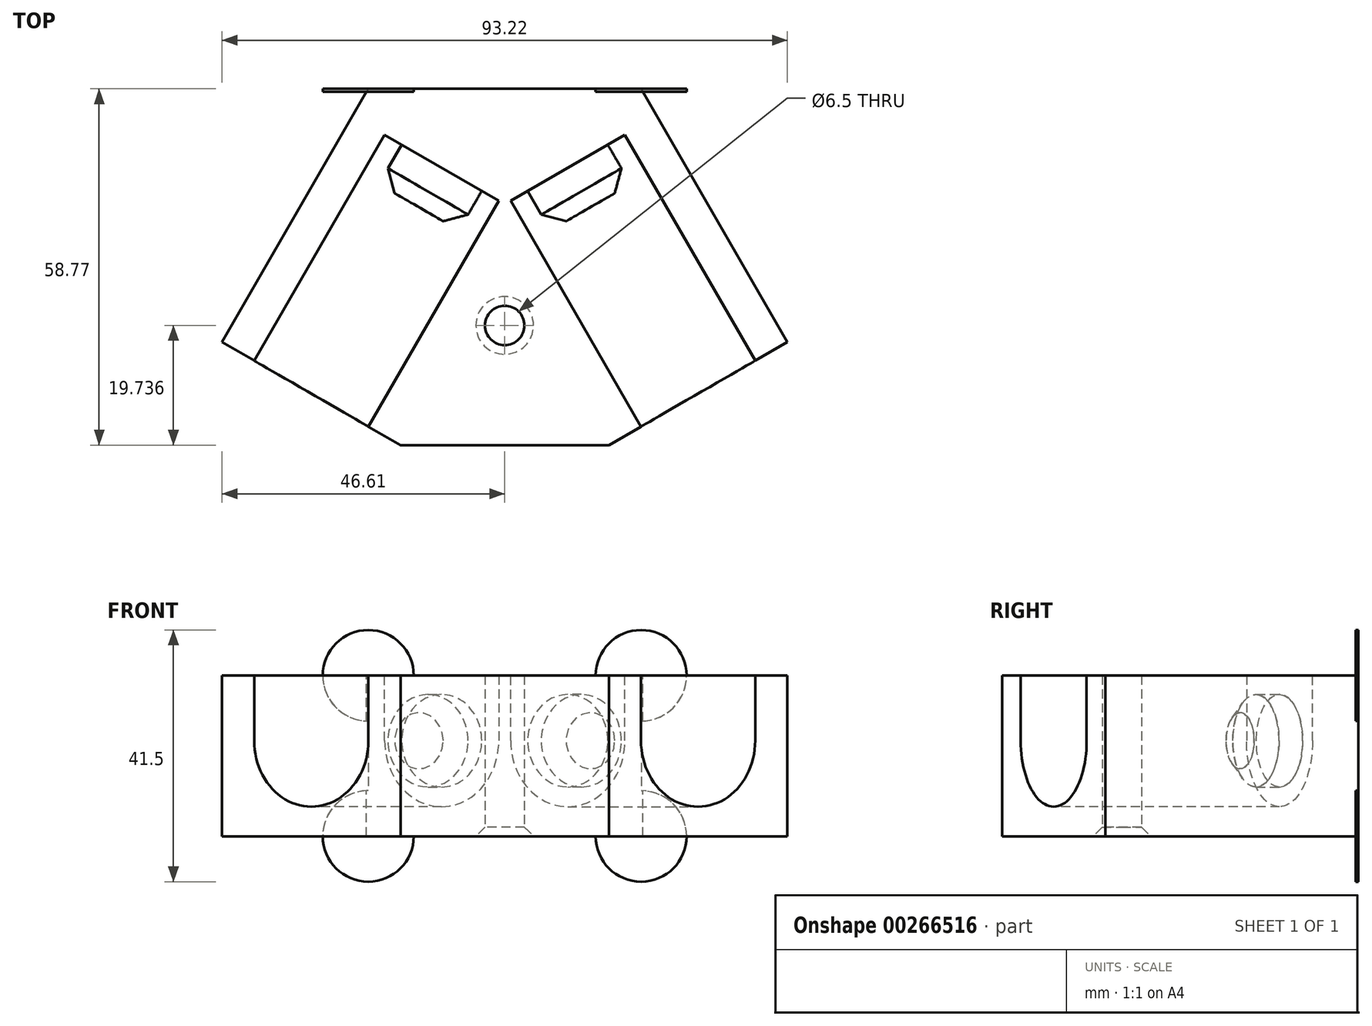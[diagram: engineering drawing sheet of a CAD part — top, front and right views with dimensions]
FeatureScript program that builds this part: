
annotation { "Feature Type Name" : "Feature", "Feature Type Description" : "" }
export const myFeature = defineFeature(function(context is Context, id is Id, definition is map)
    precondition{}
    {
        {
            var Q0;
            Q0=qCreatedBy(makeId("Top.planeOp"),FACE);
            var sketch = newSketch(context, id + "F0", { "sketchPlane" : qUnion([Q0])});
            skCircle(sketch, "E0", {"center": v(0, 0) * mm, "radius": 199.98 * mm, "construction": true});
            skLineSegment(sketch, "E1", {"start": v(0, 199.98) * mm, "end": v(-173.18, -99.99) * mm, "construction": true});
            skLineSegment(sketch, "E2", {"start": v(-173.18, -99.99) * mm, "end": v(173.18, -99.99) * mm, "construction": true});
            skLineSegment(sketch, "E3", {"start": v(173.18, -99.99) * mm, "end": v(0, 199.98) * mm, "construction": true});
            skLineSegment(sketch, "E4", {"start": v(0, 0) * mm, "end": v(-173.18, -99.99) * mm, "construction": true});
            skLineSegment(sketch, "E5", {"start": v(-152.4, -87.99) * mm, "end": v(-152.4, -99.99) * mm, "construction": true});
            skLineSegment(sketch, "E6", {"start": v(-152.4, -87.99) * mm, "end": v(0, -87.99) * mm, "construction": true});
            skLineSegment(sketch, "E7", {"start": v(0, -87.99) * mm, "end": v(0, 0) * mm, "construction": true});
            skLineSegment(sketch, "E8", {"start": v(0, 199.98) * mm, "end": v(0, 0) * mm, "construction": true});
            skLineSegment(sketch, "E9", {"start": v(-20.78, 187.98) * mm, "end": v(0, 175.98) * mm, "construction": true});
            skLineSegment(sketch, "E10", {"start": v(-20.78, 187.98) * mm, "end": v(-42.28, 150.74) * mm, "construction": true});
            skCircle(sketch, "E11", {"center": v(0, 155.98) * mm, "radius": 3.25 * mm});
            skLineSegment(sketch, "E12", {"start": v(0, 175.98) * mm, "end": v(-28.23, 127.08) * mm, "construction": true});
            skLineSegment(sketch, "E13", {"start": v(-22.5, 195) * mm, "end": v(-46.61, 153.24) * mm});
            skLineSegment(sketch, "E14", {"start": v(-46.61, 153.24) * mm, "end": v(-17.17, 136.24) * mm});
            skLineSegment(sketch, "E15.MirrorCS", {"start": v(46.61, 153.24) * mm, "end": v(17.17, 136.24) * mm});
            skLineSegment(sketch, "E16.MirrorCS", {"start": v(22.5, 195) * mm, "end": v(46.61, 153.24) * mm});
            skLineSegment(sketch, "E17", {"start": v(-22.5, 195) * mm, "end": v(22.5, 195) * mm});
            skLineSegment(sketch, "E18", {"start": v(-17.17, 136.24) * mm, "end": v(17.17, 136.24) * mm});
            skSolve(sketch);
        }
        {
            var Q0;
            Q0 = qSketchRegion(id + "F0", true);
            extrude(context, id + "F1", {"entities" : qUnion([Q0]), "depth" : 31.5 * mm});
        }
        {
            var Q0;
            Q0=makeQuery(id+"F1.opExtrude","SWEPT_FACE",FACE,{"disambiguationData":[OSD([sQuery(id+"F0.wireOp",EDGE,"E14")])]});
            var sketch = newSketch(context, id + "F2", { "sketchPlane" : qUnion([Q0])});
            skLineSegment(sketch, "E19", {"start": v(-99.99, 31.5) * mm, "end": v(-99.99, 0) * mm, "construction": true});
            skArc(sketch, "E20", {"start": v(-110.86, 15.75) * mm, "mid": v(-99.99, 4.87) * mm, "end": v(-89.11, 15.75) * mm});
            skPoint(sketch, "E20.startSnap0", {"position": v(-99.99, 15.75) * mm});
            skLineSegment(sketch, "E21", {"start": v(-110.86, 15.75) * mm, "end": v(-110.86, 31.5) * mm});
            skLineSegment(sketch, "E22", {"start": v(-110.86, 31.5) * mm, "end": v(-89.11, 31.5) * mm});
            skLineSegment(sketch, "E23", {"start": v(-89.11, 31.5) * mm, "end": v(-89.11, 15.75) * mm});
            skSolve(sketch);
        }
        {
            var Q0;
            Q0 = qSketchRegion(id + "F2", true);
            extrude(context, id + "F3", {"entities" : qUnion([Q0]), "operationType" : NewBodyOperationType.REMOVE, "oppositeDirection" : true, "depth" : 43 * mm});
        }
        {
            var Q0;
            Q0=makeQuery(id+"F1.opExtrude","SWEPT_FACE",FACE,{"disambiguationData":[OSD([sQuery(id+"F0.wireOp",EDGE,"E15.MirrorCS")])]});
            var sketch = newSketch(context, id + "F4", { "sketchPlane" : qUnion([Q0])});
            skLineSegment(sketch, "E24", {"start": v(99.99, 31.5) * mm, "end": v(99.99, 0) * mm, "construction": true});
            skArc(sketch, "E25", {"start": v(89.11, 15.75) * mm, "mid": v(99.99, 4.87) * mm, "end": v(110.86, 15.75) * mm});
            skPoint(sketch, "E25.startSnap0", {"position": v(99.99, 15.75) * mm});
            skLineSegment(sketch, "E26", {"start": v(89.11, 15.75) * mm, "end": v(89.11, 31.5) * mm});
            skLineSegment(sketch, "E27.MirrorCS", {"start": v(110.86, 15.75) * mm, "end": v(110.86, 31.5) * mm});
            skLineSegment(sketch, "E28", {"start": v(89.11, 31.5) * mm, "end": v(110.86, 31.5) * mm});
            skSolve(sketch);
        }
        {
            var Q0;
            Q0 = qSketchRegion(id + "F4", true);
            extrude(context, id + "F5", {"entities" : qUnion([Q0]), "operationType" : NewBodyOperationType.REMOVE, "oppositeDirection" : true, "depth" : 43 * mm});
        }
        {
            var Q0;
            Q0=makeQuery(id+"F3.boolean.opBoolean","COPY",FACE,{"derivedFrom":makeQuery(id+"F3.opExtrude","CAP_FACE",FACE,{"disambiguationData":[OSD([sQuery(id+"F2.wireOp",EDGE,"E20"),sQuery(id+"F2.wireOp",EDGE,"E21"),sQuery(id+"F2.wireOp",EDGE,"E22"),sQuery(id+"F2.wireOp",EDGE,"E23")])],"isStart":false})});
            var sketch = newSketch(context, id + "F6", { "sketchPlane" : qUnion([Q0])});
            skCircle(sketch, "E29", {"center": v(-99.99, 15.75) * mm, "radius": 7.62 * mm});
            skSolve(sketch);
        }
        {
            var Q0;
            Q0 = qSketchRegion(id + "F6", true);
            extrude(context, id + "F7", {"entities" : qUnion([Q0]), "operationType" : NewBodyOperationType.ADD, "depth" : 7.5 * mm});
        }
        {
            var Q0;
            Q0=makeQuery(id+"F5.boolean.opBoolean","COPY",FACE,{"derivedFrom":makeQuery(id+"F5.opExtrude","CAP_FACE",FACE,{"disambiguationData":[OSD([sQuery(id+"F4.wireOp",EDGE,"E25"),sQuery(id+"F4.wireOp",EDGE,"E26"),sQuery(id+"F4.wireOp",EDGE,"E27.MirrorCS"),sQuery(id+"F4.wireOp",EDGE,"E28")])],"isStart":false})});
            var sketch = newSketch(context, id + "F8", { "sketchPlane" : qUnion([Q0])});
            skCircle(sketch, "E30", {"center": v(99.99, 15.75) * mm, "radius": 7.62 * mm});
            skSolve(sketch);
        }
        {
            var Q0;
            Q0 = qSketchRegion(id + "F8", true);
            extrude(context, id + "F9", {"entities" : qUnion([Q0]), "operationType" : NewBodyOperationType.ADD, "depth" : 7.5 * mm});
        }
        {
            var Q0;
            Q0=makeQuery(id+"F7.opExtrude","CAP_EDGE",EDGE,{"disambiguationData":[OSD([sQuery(id+"F6.wireOp",EDGE,"E29")])],"isStart":false});
            var Q1;
            Q1=makeQuery(id+"F9.opExtrude","CAP_EDGE",EDGE,{"disambiguationData":[OSD([sQuery(id+"F8.wireOp",EDGE,"E30")])],"isStart":false});
            chamfer(context, id + "F10", {"entities" : qUnion([Q0, Q1]), "width" : 3 * mm, "tangentPropagation" : true});
        }
        {
            var Q0;
            Q0=makeQuery(id+"F1.opExtrude","CAP_FACE",FACE,{"disambiguationData":[OSD([sQuery(id+"F0.wireOp",EDGE,"E11"),sQuery(id+"F0.wireOp",EDGE,"E13"),sQuery(id+"F0.wireOp",EDGE,"E14"),sQuery(id+"F0.wireOp",EDGE,"E15.MirrorCS"),sQuery(id+"F0.wireOp",EDGE,"E16.MirrorCS"),sQuery(id+"F0.wireOp",EDGE,"E17"),sQuery(id+"F0.wireOp",EDGE,"E18")])],"isStart":false});
            extrude(context, id + "F11", {"entities" : qUnion([Q0]), "operationType" : NewBodyOperationType.REMOVE, "oppositeDirection" : true, "depth" : 5 * mm});
        }
        {
            var Q0;
            Q0=makeQuery(id+"F11.boolean.opBoolean","COPY",EDGE,{"derivedFrom":makeQuery(id+"F11.opExtrude","CAP_EDGE",EDGE,{"disambiguationData":[OSD([sQuery(id+"F0.wireOp",EDGE,"E11")])],"isStart":false})});
            var Q1;
            Q1=makeQuery(id+"F1.opExtrude","CAP_EDGE",EDGE,{"disambiguationData":[OSD([sQuery(id+"F0.wireOp",EDGE,"E11")])],"isStart":true});
            chamfer(context, id + "F12", {"entities" : qUnion([Q0, Q1]), "width" : 1.5 * mm, "tangentPropagation" : true});
        }
        {
            var Q0;
            Q0=makeQuery(id+"F1.opExtrude","SWEPT_FACE",FACE,{"disambiguationData":[OSD([sQuery(id+"F0.wireOp",EDGE,"E17")])]});
            var sketch = newSketch(context, id + "F13", { "sketchPlane" : qUnion([Q0])});
            skCircle(sketch, "E31", {"center": v(-22.5, 26.5) * mm, "radius": 7.5 * mm});
            skCircle(sketch, "E32", {"center": v(22.5, 26.5) * mm, "radius": 7.5 * mm});
            skCircle(sketch, "E33", {"center": v(22.5, 0) * mm, "radius": 7.5 * mm});
            skCircle(sketch, "E34", {"center": v(-22.5, 0) * mm, "radius": 7.5 * mm});
            skSolve(sketch);
        }
        {
            var Q0;
            Q0 = qSketchRegion(id + "F13", true);
            extrude(context, id + "F14", {"entities" : qUnion([Q0]), "operationType" : NewBodyOperationType.ADD, "oppositeDirection" : true, "depth" : 0.5 * mm});
        }
    });
